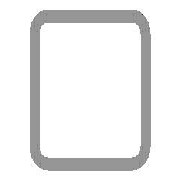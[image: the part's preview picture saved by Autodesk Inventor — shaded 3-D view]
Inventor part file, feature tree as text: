
AUTODESK INVENTOR PART (.ipt)
format: ipt  version: 2025.1 (Build 291241020, 241B)  size: 137,216 bytes
history: native  units: mm (DEFAULTED — no unit token found)
features: other x3, sketch x1, plane x1
ambient origin geometry x8: Origin, YZ Plane, XZ Plane, XY Plane, X Axis, Y Axis, Z Axis, Center Point
bodies: Solid1 (feature_tree), Body (feature_tree)
feature tree (5):
  other  "Driven Length"
  other  "Start plane"
  other  "End plane"
  sketch  "Sketch3"  dims[d3=7000.0mm d4=0.0mm d7=4.5mm d10=80.0mm d11=80.0mm d12=3.0mm d13=-0.0mm d14=7000.0mm d15=40.0mm d16=40.0mm d17=90.0deg d18=7000.0mm d19=3.0mm d20=3.0mm]
  plane  "Work Plane3"
